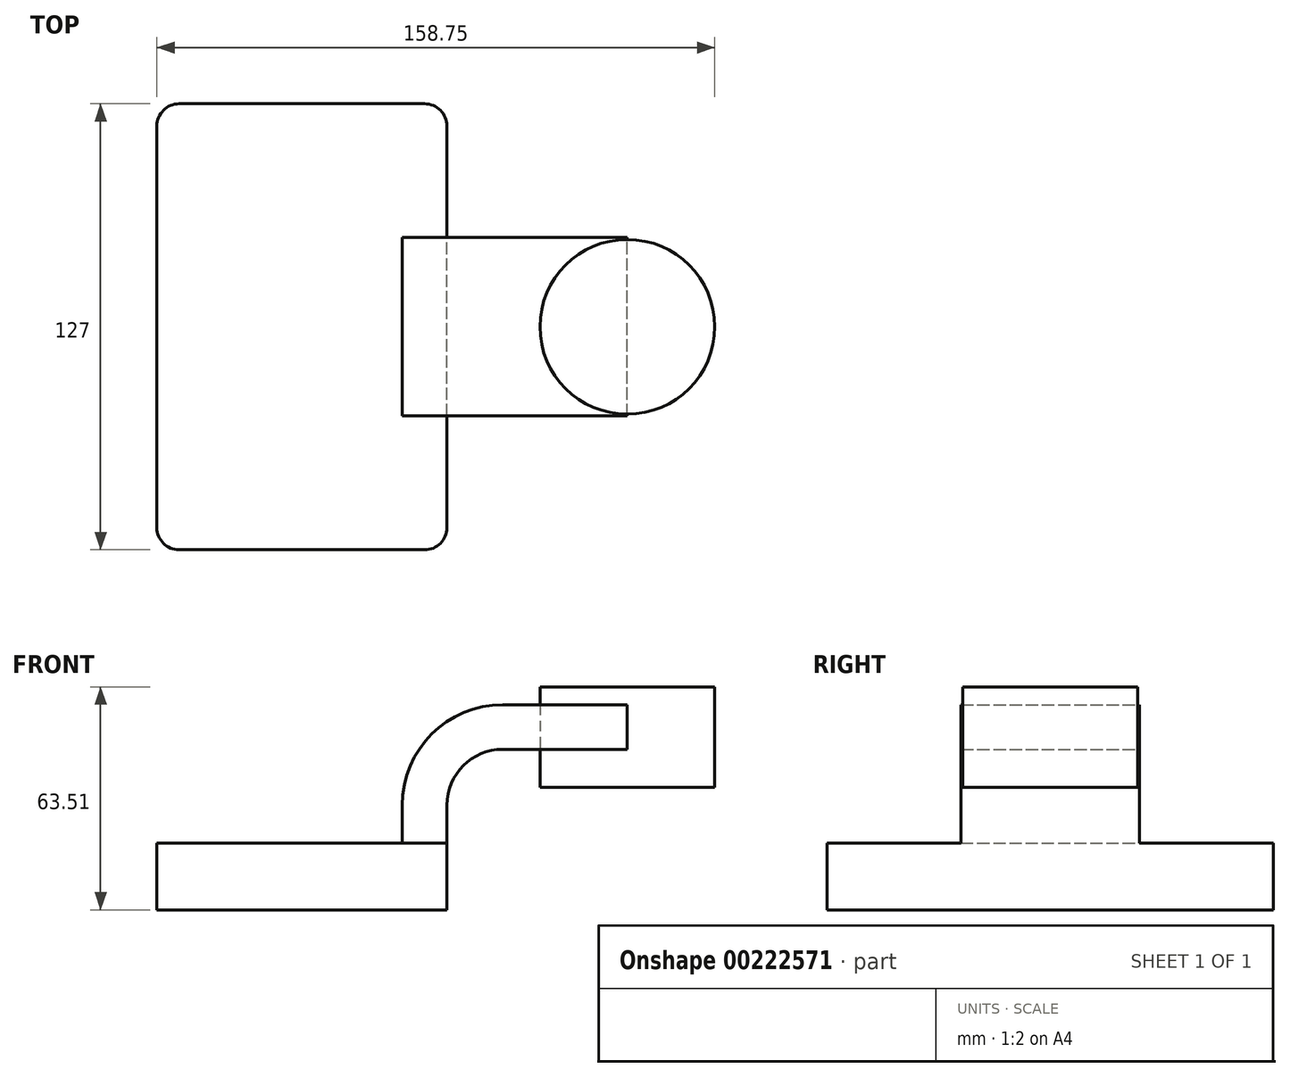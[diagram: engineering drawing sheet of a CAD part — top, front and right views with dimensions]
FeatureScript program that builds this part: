
annotation { "Feature Type Name" : "Feature", "Feature Type Description" : "" }
export const myFeature = defineFeature(function(context is Context, id is Id, definition is map)
    precondition{}
    {
        {
            var Q0;
            Q0=qCreatedBy(makeId("Front.planeOp"),FACE);
            var sketch = newSketch(context, id + "F0", { "sketchPlane" : qUnion([Q0])});
            skLineSegment(sketch, "E0.bottom", {"start": v(-41.28, 9.52) * mm, "end": v(41.27, 9.53) * mm});
            skLineSegment(sketch, "E0.top", {"start": v(-41.28, -9.52) * mm, "end": v(41.28, -9.52) * mm});
            skLineSegment(sketch, "E0.left", {"start": v(-41.28, 9.52) * mm, "end": v(-41.28, -9.53) * mm});
            skLineSegment(sketch, "E0.right", {"start": v(41.27, 9.53) * mm, "end": v(41.28, -9.52) * mm});
            skPoint(sketch, "E0.middle", {"position": v(0, 0) * mm});
            skLineSegment(sketch, "E1.bottom", {"start": v(66.67, 53.98) * mm, "end": v(117.47, 53.98) * mm});
            skLineSegment(sketch, "E1.top", {"start": v(66.67, 25.4) * mm, "end": v(117.47, 25.4) * mm});
            skLineSegment(sketch, "E1.left", {"start": v(66.67, 53.98) * mm, "end": v(66.67, 25.4) * mm});
            skLineSegment(sketch, "E1.right", {"start": v(117.47, 53.98) * mm, "end": v(117.47, 25.4) * mm});
            skPoint(sketch, "E1.middle", {"position": v(92.07, 39.69) * mm});
            skLineSegment(sketch, "E2", {"start": v(41.27, 9.53) * mm, "end": v(41.27, 20.32) * mm});
            skArc(sketch, "E3", {"start": v(41.27, 20.32) * mm, "mid": v(45.92, 31.55) * mm, "end": v(57.15, 36.2) * mm});
            skLineSegment(sketch, "E4", {"start": v(57.15, 36.2) * mm, "end": v(92.61, 36.2) * mm});
            skLineSegment(sketch, "E5.0", {"start": v(57.15, 48.9) * mm, "end": v(92.61, 48.9) * mm});
            skArc(sketch, "E5.1", {"start": v(28.57, 20.32) * mm, "mid": v(36.94, 40.53) * mm, "end": v(57.15, 48.9) * mm});
            skLineSegment(sketch, "E5.2", {"start": v(28.57, 9.53) * mm, "end": v(28.57, 20.32) * mm});
            skLineSegment(sketch, "E6", {"start": v(92.61, 25.4) * mm, "end": v(92.61, 53.98) * mm});
            skFitSpline(sketch, "E7", {"points": [v(-41.28, 9.53) * mm, v(57.15, 48.9) * mm], "startDerivative": vector(102.44, 84.74) * mm, "endDerivative": vector(127.3, -9.41) * mm});
            skSolve(sketch);
        }
        {
            var Q0;
            Q0=makeQuery(id+"F0.imprint","IMPRINT",FACE,{"disambiguationData":[TD([[makeQuery(id+"F0.imprint","IMPRINT",EDGE,{"derivedFrom":sQuery(id+"F0.wireOp",EDGE,"E0.top")}),1.0]])]});
            extrude(context, id + "F1", {"entities" : qUnion([Q0]), "endBound" : BoundingType.SYMMETRIC, "depth" : 127 * mm});
        }
        {
            var Q0;
            {var subQ1=sQuery(id+"F0.wireOp",EDGE,"E2");Q0=makeQuery(id+"F0.imprint","IMPRINT",FACE,{"disambiguationData":[TD([[makeQuery(id+"F0.imprint","IMPRINT",EDGE,{"derivedFrom":subQ1}),1.0]])]});}
            var Q1;
            {var subQ0=sQuery(id+"F0.wireOp",EDGE,"E5.0");var subQ1=sQuery(id+"F0.wireOp",EDGE,"E1.left");var subQ2=makeQuery(id+"F0.imprint","INTERSECT",VERTEX,{"derivedFrom":[subQ1,subQ0]});Q1=makeQuery(id+"F0.imprint","IMPRINT",FACE,{"disambiguationData":[TD([[makeQuery(id+"F0.imprint","IMPRINT",EDGE,{"disambiguationData":[TD([[subQ2,-1.0]])],"derivedFrom":subQ1}),1.0]])]});}
            extrude(context, id + "F2", {"entities" : qUnion([Q0, Q1]), "operationType" : NewBodyOperationType.ADD, "endBound" : BoundingType.SYMMETRIC, "depth" : 50.8 * mm});
        }
        {
            var Q0;
            Q0=makeQuery(id+"F0.imprint","IMPRINT",FACE,{"disambiguationData":[TD([[makeQuery(id+"F0.imprint","IMPRINT",EDGE,{"derivedFrom":sQuery(id+"F0.wireOp",EDGE,"E5.1")}),1.0]])]});
            extrude(context, id + "F3", {"entities" : qUnion([Q0]), "operationType" : NewBodyOperationType.ADD, "endBound" : BoundingType.SYMMETRIC, "depth" : 15.88 * mm});
        }
        {
            var Q0;
            {var subQ0=sQuery(id+"F0.wireOp",EDGE,"E1.right");Q0=makeQuery(id+"F0.imprint","IMPRINT",FACE,{"disambiguationData":[TD([[makeQuery(id+"F0.imprint","IMPRINT",EDGE,{"derivedFrom":subQ0}),-1.0]])]});}
            var Q1;
            Q1=sQuery(id+"F0.wireOp",EDGE,"E6");
            revolve(context, id + "F4", {"entities" : qUnion([Q0]), "axis" : qUnion([Q1]), "revolveType" : RevolveType.FULL});
        }
        {
            var Q0;
            Q0=makeQuery(id+"F1.opExtrude","CAP_EDGE",EDGE,{"disambiguationData":[OSD([sQuery(id+"F0.wireOp",EDGE,"E0.right")])],"isStart":false});
            var Q1;
            Q1=makeQuery(id+"F1.opExtrude","CAP_EDGE",EDGE,{"disambiguationData":[OSD([sQuery(id+"F0.wireOp",EDGE,"E0.left")])],"isStart":false});
            var Q2;
            Q2=makeQuery(id+"F1.opExtrude","CAP_EDGE",EDGE,{"disambiguationData":[OSD([sQuery(id+"F0.wireOp",EDGE,"E0.right")])],"isStart":true});
            var Q3;
            Q3=makeQuery(id+"F1.opExtrude","CAP_EDGE",EDGE,{"disambiguationData":[OSD([sQuery(id+"F0.wireOp",EDGE,"E0.left")])],"isStart":true});
            fillet(context, id + "F5", {"entities" : qUnion([Q0, Q1, Q2, Q3]), "radius" : 6.35 * mm, "tangentPropagation" : true, "allowEdgeOverflow" : false});
        }
    });
